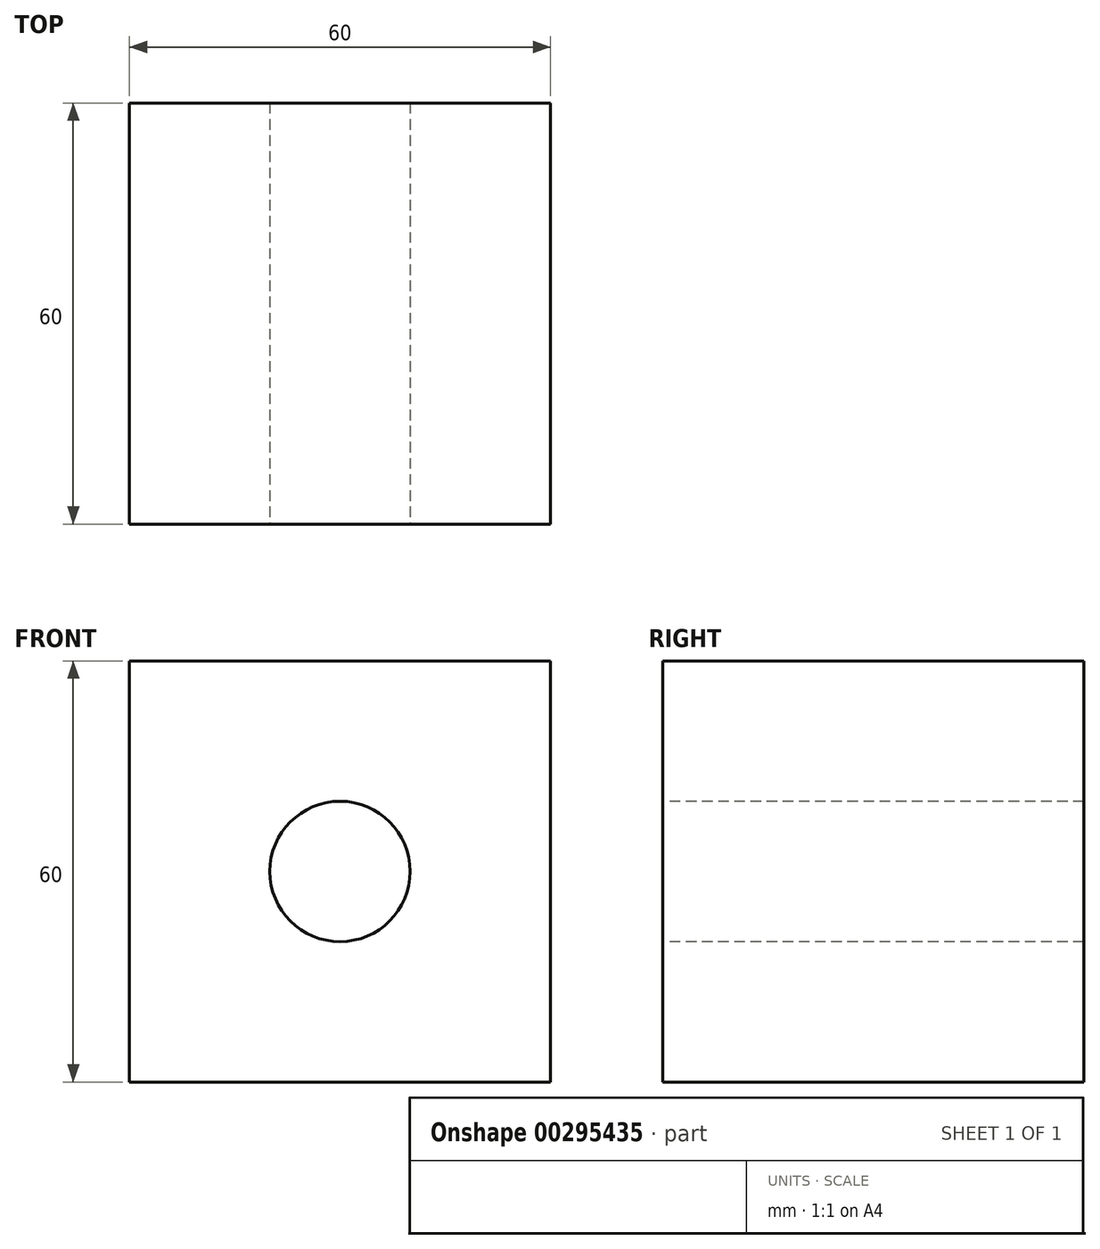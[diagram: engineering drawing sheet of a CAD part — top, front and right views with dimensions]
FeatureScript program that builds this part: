
annotation { "Feature Type Name" : "Feature", "Feature Type Description" : "" }
export const myFeature = defineFeature(function(context is Context, id is Id, definition is map)
    precondition{}
    {
        {
            var Q0;
            Q0=qCreatedBy(makeId("Front.planeOp"),FACE);
            var sketch = newSketch(context, id + "F0", { "sketchPlane" : qUnion([Q0])});
            skLineSegment(sketch, "E0.bottom", {"start": v(30, 30) * mm, "end": v(-30, 30) * mm});
            skLineSegment(sketch, "E0.top", {"start": v(30, -30) * mm, "end": v(-30, -30) * mm});
            skLineSegment(sketch, "E0.left", {"start": v(30, 30) * mm, "end": v(30, -30) * mm});
            skLineSegment(sketch, "E0.right", {"start": v(-30, 30) * mm, "end": v(-30, -30) * mm});
            skPoint(sketch, "E0.middle", {"position": v(0, 0) * mm});
            skSolve(sketch);
        }
        {
            var Q0;
            Q0 = qSketchRegion(id + "F0", true);
            extrude(context, id + "F1", {"entities" : qUnion([Q0]), "depth" : 60 * mm});
        }
        {
            var Q0;
            Q0=makeQuery(id+"F1.opExtrude","CAP_FACE",FACE,{"disambiguationData":[OSD([sQuery(id+"F0.wireOp",EDGE,"E0.bottom"),sQuery(id+"F0.wireOp",EDGE,"E0.top"),sQuery(id+"F0.wireOp",EDGE,"E0.left"),sQuery(id+"F0.wireOp",EDGE,"E0.right")])],"isStart":false});
            var sketch = newSketch(context, id + "F2", { "sketchPlane" : qUnion([Q0])});
            skCircle(sketch, "E1", {"center": v(0, 0) * mm, "radius": 10 * mm});
            skSolve(sketch);
        }
        {
            var Q0;
            Q0 = qSketchRegion(id + "F2", true);
            extrude(context, id + "F3", {"entities" : qUnion([Q0]), "operationType" : NewBodyOperationType.REMOVE, "endBound" : BoundingType.THROUGH_ALL, "oppositeDirection" : true, "depth" : 25 * mm});
        }
    });
